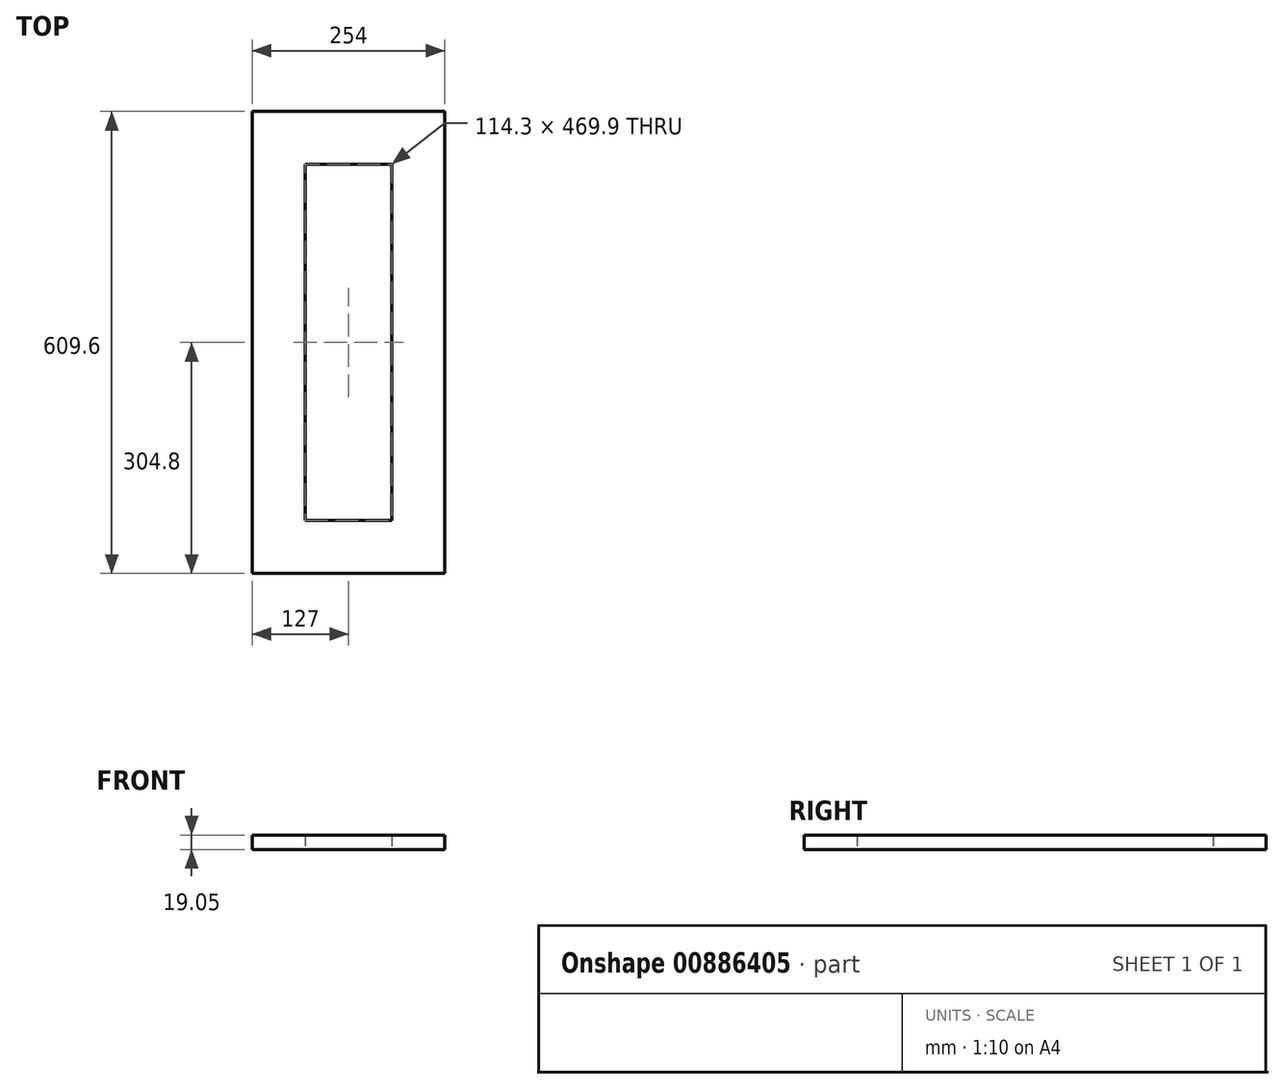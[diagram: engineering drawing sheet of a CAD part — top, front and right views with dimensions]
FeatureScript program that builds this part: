
annotation { "Feature Type Name" : "Feature", "Feature Type Description" : "" }
export const myFeature = defineFeature(function(context is Context, id is Id, definition is map)
    precondition{}
    {
        {
            var Q0;
            Q0=qCreatedBy(makeId("Top.planeOp"),FACE);
            var sketch = newSketch(context, id + "F0", { "sketchPlane" : qUnion([Q0])});
            skLineSegment(sketch, "E0.bottom", {"start": v(127, 304.8) * mm, "end": v(-127, 304.8) * mm});
            skLineSegment(sketch, "E0.top", {"start": v(127, -304.8) * mm, "end": v(-127, -304.8) * mm});
            skLineSegment(sketch, "E0.left", {"start": v(127, 304.8) * mm, "end": v(127, -304.8) * mm});
            skLineSegment(sketch, "E0.right", {"start": v(-127, 304.8) * mm, "end": v(-127, -304.8) * mm});
            skPoint(sketch, "E0.middle", {"position": v(0, 0) * mm});
            skLineSegment(sketch, "E1.bottom", {"start": v(57.15, 234.95) * mm, "end": v(-57.15, 234.95) * mm});
            skLineSegment(sketch, "E1.top", {"start": v(57.15, -234.95) * mm, "end": v(-57.15, -234.95) * mm});
            skLineSegment(sketch, "E1.left", {"start": v(57.15, 234.95) * mm, "end": v(57.15, -234.95) * mm});
            skLineSegment(sketch, "E1.right", {"start": v(-57.15, 234.95) * mm, "end": v(-57.15, -234.95) * mm});
            skSolve(sketch);
        }
        {
            var Q0;
            Q0=makeQuery(id+"F0.imprint","IMPRINT",FACE,{"disambiguationData":[TD([[makeQuery(id+"F0.imprint","IMPRINT",EDGE,{"derivedFrom":sQuery(id+"F0.wireOp",EDGE,"E0.bottom")}),1.0]])]});
            extrude(context, id + "F1", {"entities" : qUnion([Q0]), "depth" : 19.05 * mm, "offsetDistance" : 25.4 * mm});
        }
    });
